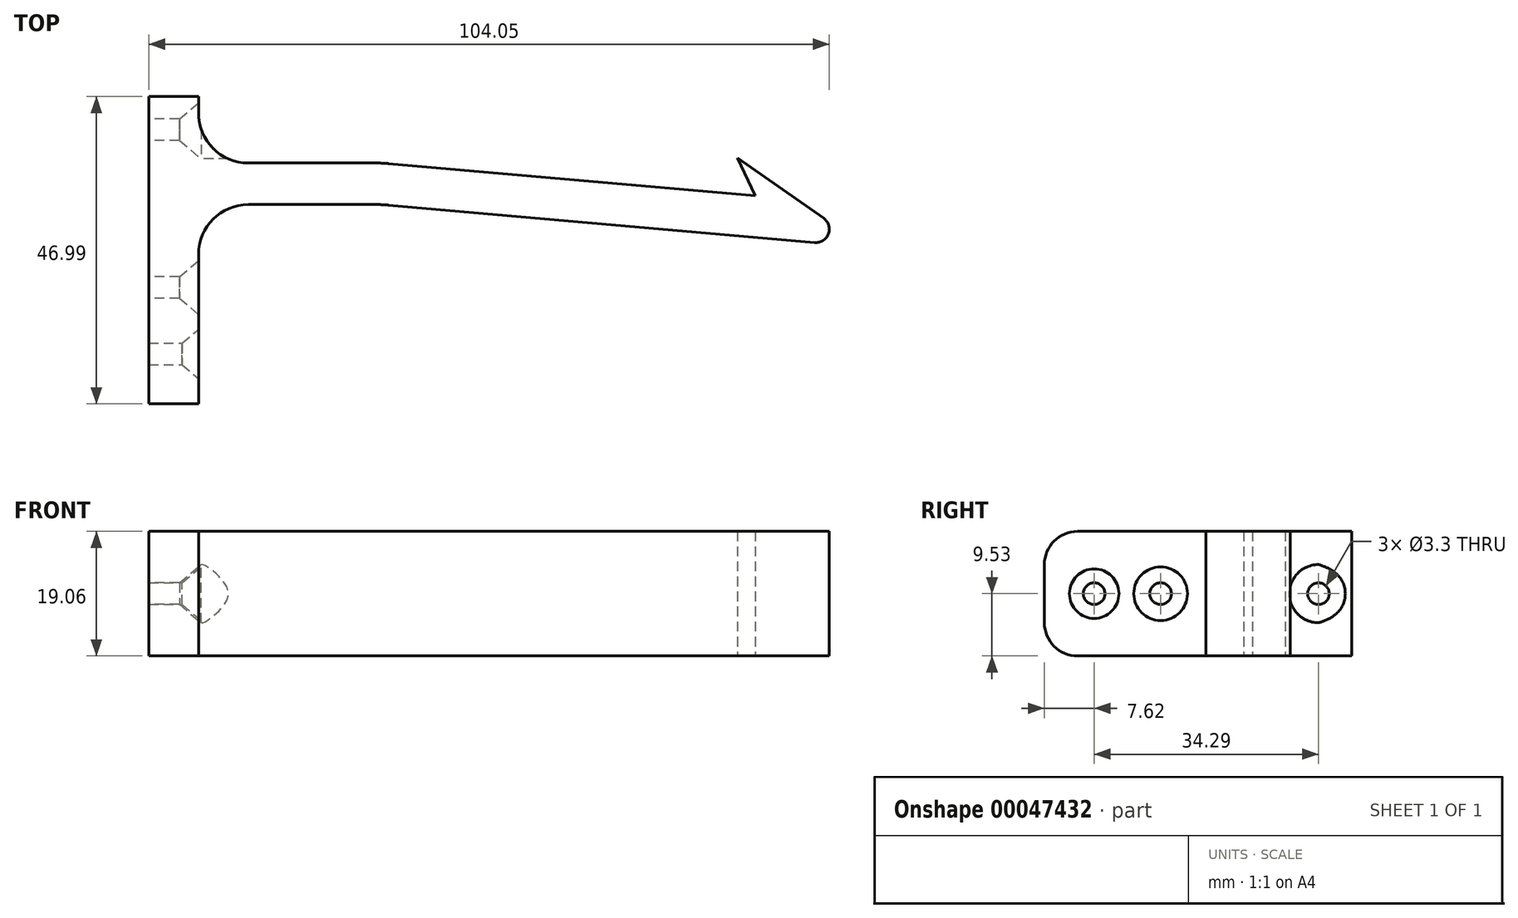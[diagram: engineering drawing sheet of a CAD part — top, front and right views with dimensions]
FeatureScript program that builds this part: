
annotation { "Feature Type Name" : "Feature", "Feature Type Description" : "" }
export const myFeature = defineFeature(function(context is Context, id is Id, definition is map)
    precondition{}
    {
        {
            var Q0;
            Q0=qCreatedBy(makeId("Top.planeOp"),FACE);
            var sketch = newSketch(context, id + "F0", { "sketchPlane" : qUnion([Q0])});
            skLineSegment(sketch, "E0", {"start": v(0, -36.83) * mm, "end": v(7.62, -36.83) * mm});
            skLineSegment(sketch, "E1", {"start": v(7.62, -36.83) * mm, "end": v(7.62, -13.97) * mm});
            skLineSegment(sketch, "E2", {"start": v(103.19, -8.46) * mm, "end": v(90.03, 0.76) * mm});
            skLineSegment(sketch, "E3", {"start": v(90.03, 0.76) * mm, "end": v(92.71, -5) * mm});
            skLineSegment(sketch, "E4", {"start": v(0, 0) * mm, "end": v(0, -36.83) * mm});
            skPoint(sketch, "E5.visualSharp", {"position": v(7.62, -6.35) * mm});
            skPoint(sketch, "E6.visualSharp", {"position": v(127, -25.13) * mm});
            skArc(sketch, "E6.filletArc", {"start": v(101.84, -12.15) * mm, "mid": v(103.93, -10.82) * mm, "end": v(103.19, -8.46) * mm});
            skArc(sketch, "E7.filletArc", {"start": v(15.24, -6.35) * mm, "mid": v(9.85, -8.58) * mm, "end": v(7.62, -13.97) * mm});
            skLineSegment(sketch, "E8", {"start": v(15.24, 0) * mm, "end": v(34.45, 0) * mm});
            skLineSegment(sketch, "E9", {"start": v(36.66, -0.1) * mm, "end": v(92.71, -5) * mm});
            skLineSegment(sketch, "E10", {"start": v(15.24, -6.35) * mm, "end": v(34.45, -6.35) * mm});
            skLineSegment(sketch, "E11", {"start": v(36.66, -6.45) * mm, "end": v(101.84, -12.15) * mm});
            skLineSegment(sketch, "E12", {"start": v(35.56, 0) * mm, "end": v(35.56, -6.35) * mm, "construction": true});
            skPoint(sketch, "E13.visualSharp", {"position": v(35.56, 0) * mm});
            skArc(sketch, "E13.filletArc", {"start": v(36.66, -0.1) * mm, "mid": v(35.56, -0.02) * mm, "end": v(34.45, 0) * mm});
            skPoint(sketch, "E14.visualSharp", {"position": v(35.56, -6.35) * mm});
            skArc(sketch, "E14.filletArc", {"start": v(36.66, -6.45) * mm, "mid": v(35.56, -6.37) * mm, "end": v(34.45, -6.35) * mm});
            skLineSegment(sketch, "E15", {"start": v(0, 0) * mm, "end": v(0, 10.16) * mm});
            skLineSegment(sketch, "E16", {"start": v(0, 10.16) * mm, "end": v(7.62, 10.16) * mm});
            skLineSegment(sketch, "E17", {"start": v(7.62, 10.16) * mm, "end": v(7.62, 7.62) * mm});
            skPoint(sketch, "E18.visualSharp", {"position": v(7.62, 0) * mm});
            skArc(sketch, "E18.filletArc", {"start": v(7.62, 7.62) * mm, "mid": v(9.85, 2.23) * mm, "end": v(15.24, 0) * mm});
            skSolve(sketch);
        }
        {
            var Q0;
            Q0=makeQuery(id+"F0.imprint","IMPRINT",FACE,{"disambiguationData":[TD([[makeQuery(id+"F0.imprint","IMPRINT",EDGE,{"derivedFrom":sQuery(id+"F0.wireOp",EDGE,"E0")}),1.0]])]});
            extrude(context, id + "F1", {"entities" : qUnion([Q0]), "endBound" : BoundingType.SYMMETRIC, "depth" : 19.05 * mm});
        }
        {
            var Q0;
            Q0=qCreatedBy(makeId("Top.planeOp"),FACE);
            var sketch = newSketch(context, id + "F2", { "sketchPlane" : qUnion([Q0])});
            skLineSegment(sketch, "E19", {"start": v(0, -20.7) * mm, "end": v(4.7, -20.7) * mm});
            skLineSegment(sketch, "E20", {"start": v(4.7, -20.7) * mm, "end": v(9.65, -24.86) * mm});
            skLineSegment(sketch, "E21", {"start": v(9.65, -24.86) * mm, "end": v(9.65, -19.05) * mm, "construction": true});
            skLineSegment(sketch, "E22", {"start": v(9.65, -19.05) * mm, "end": v(0, -19.05) * mm});
            skLineSegment(sketch, "E23", {"start": v(0, -19.05) * mm, "end": v(0, -20.7) * mm});
            skArc(sketch, "E24.0", {"start": v(15.24, -6.35) * mm, "mid": v(9.85, -8.58) * mm, "end": v(7.62, -13.97) * mm, "construction": true});
            skLineSegment(sketch, "E25", {"start": v(9.65, -19.05) * mm, "end": v(9.65, -8.79) * mm, "construction": true});
            skLineSegment(sketch, "E26", {"start": v(0, -19.05) * mm, "end": v(-5, -19.05) * mm, "construction": true});
            skLineSegment(sketch, "E27.MirrorCS", {"start": v(0, -17.4) * mm, "end": v(4.7, -17.4) * mm, "construction": true});
            skLineSegment(sketch, "E28.MirrorCS", {"start": v(4.7, -17.4) * mm, "end": v(9.65, -13.24) * mm, "construction": true});
            skLineSegment(sketch, "E29", {"start": v(9.65, -19.05) * mm, "end": v(11.56, -19.05) * mm});
            skLineSegment(sketch, "E30", {"start": v(11.56, -19.05) * mm, "end": v(11.56, -24.86) * mm});
            skLineSegment(sketch, "E31", {"start": v(11.56, -24.86) * mm, "end": v(9.65, -24.86) * mm});
            skSolve(sketch);
        }
        {
            var Q0;
            Q0=qSketchRegion(id+"F2",true);
            var Q1;
            Q1=sQuery(id+"F2.wireOp",EDGE,"E26");
            revolve(context, id + "F3", {"operationType" : NewBodyOperationType.REMOVE, "entities" : qUnion([Q0]), "axis" : qUnion([Q1]), "revolveType" : RevolveType.FULL, "oppositeDirection" : true});
        }
        {
            var Q0;
            Q0=qCreatedBy(makeId("Top.planeOp"),FACE);
            var sketch = newSketch(context, id + "F4", { "sketchPlane" : qUnion([Q0])});
            skLineSegment(sketch, "E32", {"start": v(0, -29.21) * mm, "end": v(7.62, -29.21) * mm});
            skLineSegment(sketch, "E33", {"start": v(7.62, -29.21) * mm, "end": v(7.62, -33) * mm});
            skLineSegment(sketch, "E34", {"start": v(7.62, -33) * mm, "end": v(5.08, -30.86) * mm});
            skLineSegment(sketch, "E35", {"start": v(5.08, -30.86) * mm, "end": v(0, -30.86) * mm});
            skLineSegment(sketch, "E36", {"start": v(0, -30.86) * mm, "end": v(0, -29.21) * mm});
            skLineSegment(sketch, "E37.MirrorCS", {"start": v(5.08, -27.56) * mm, "end": v(0, -27.56) * mm, "construction": true});
            skLineSegment(sketch, "E38.MirrorCS", {"start": v(7.62, -25.43) * mm, "end": v(5.08, -27.56) * mm, "construction": true});
            skSolve(sketch);
        }
        {
            var Q0;
            Q0=qSketchRegion(id+"F4",true);
            var Q1;
            Q1=sQuery(id+"F4.wireOp",EDGE,"E32");
            revolve(context, id + "F5", {"operationType" : NewBodyOperationType.REMOVE, "entities" : qUnion([Q0]), "axis" : qUnion([Q1]), "revolveType" : RevolveType.FULL, "oppositeDirection" : true});
        }
        {
            var Q0;
            Q0=makeQuery(id+"F1.opExtrude","CAP_EDGE",EDGE,{"disambiguationData":[OSD([sQuery(id+"F0.wireOp",EDGE,"E0")])],"isStart":false});
            var Q1;
            Q1=makeQuery(id+"F1.opExtrude","CAP_EDGE",EDGE,{"disambiguationData":[OSD([sQuery(id+"F0.wireOp",EDGE,"E0")])],"isStart":true});
            fillet(context, id + "F6", {"entities" : qUnion([Q0, Q1]), "radius" : 5.08 * mm, "tangentPropagation" : true, "allowEdgeOverflow" : false});
        }
        {
            var Q0;
            Q0=qCreatedBy(makeId("Top.planeOp"),FACE);
            var sketch = newSketch(context, id + "F7", { "sketchPlane" : qUnion([Q0])});
            skLineSegment(sketch, "E39", {"start": v(0, 3.43) * mm, "end": v(4.7, 3.43) * mm});
            skLineSegment(sketch, "E40", {"start": v(4.7, 3.43) * mm, "end": v(8.04, 0.63) * mm});
            skLineSegment(sketch, "E41", {"start": v(8.04, 0.63) * mm, "end": v(8.04, 5.08) * mm, "construction": true});
            skLineSegment(sketch, "E42", {"start": v(8.04, 5.08) * mm, "end": v(0, 5.08) * mm});
            skLineSegment(sketch, "E43", {"start": v(0, 5.08) * mm, "end": v(0, 3.43) * mm});
            skArc(sketch, "E44.0", {"start": v(15.24, 12.7) * mm, "mid": v(9.85, 10.47) * mm, "end": v(7.62, 5.08) * mm, "construction": true});
            skLineSegment(sketch, "E45", {"start": v(8.04, 5.08) * mm, "end": v(8.04, 7.57) * mm, "construction": true});
            skLineSegment(sketch, "E46", {"start": v(0, 5.08) * mm, "end": v(-5, 5.08) * mm, "construction": true});
            skLineSegment(sketch, "E47.MirrorCS", {"start": v(0, 6.73) * mm, "end": v(4.7, 6.73) * mm, "construction": true});
            skLineSegment(sketch, "E48.MirrorCS", {"start": v(4.7, 6.73) * mm, "end": v(8.04, 9.53) * mm, "construction": true});
            skLineSegment(sketch, "E49", {"start": v(8.04, 5.08) * mm, "end": v(15.24, 5.08) * mm});
            skLineSegment(sketch, "E50", {"start": v(15.24, 5.08) * mm, "end": v(15.24, 0.63) * mm});
            skLineSegment(sketch, "E51", {"start": v(15.24, 0.63) * mm, "end": v(8.04, 0.63) * mm});
            skSolve(sketch);
        }
        {
            var Q0;
            Q0 = qSketchRegion(id + "F7", true);
            var Q1;
            Q1=sQuery(id+"F7.wireOp",EDGE,"E42");
            revolve(context, id + "F8", {"operationType" : NewBodyOperationType.REMOVE, "entities" : qUnion([Q0]), "axis" : qUnion([Q1]), "revolveType" : RevolveType.FULL, "oppositeDirection" : true});
        }
    });
